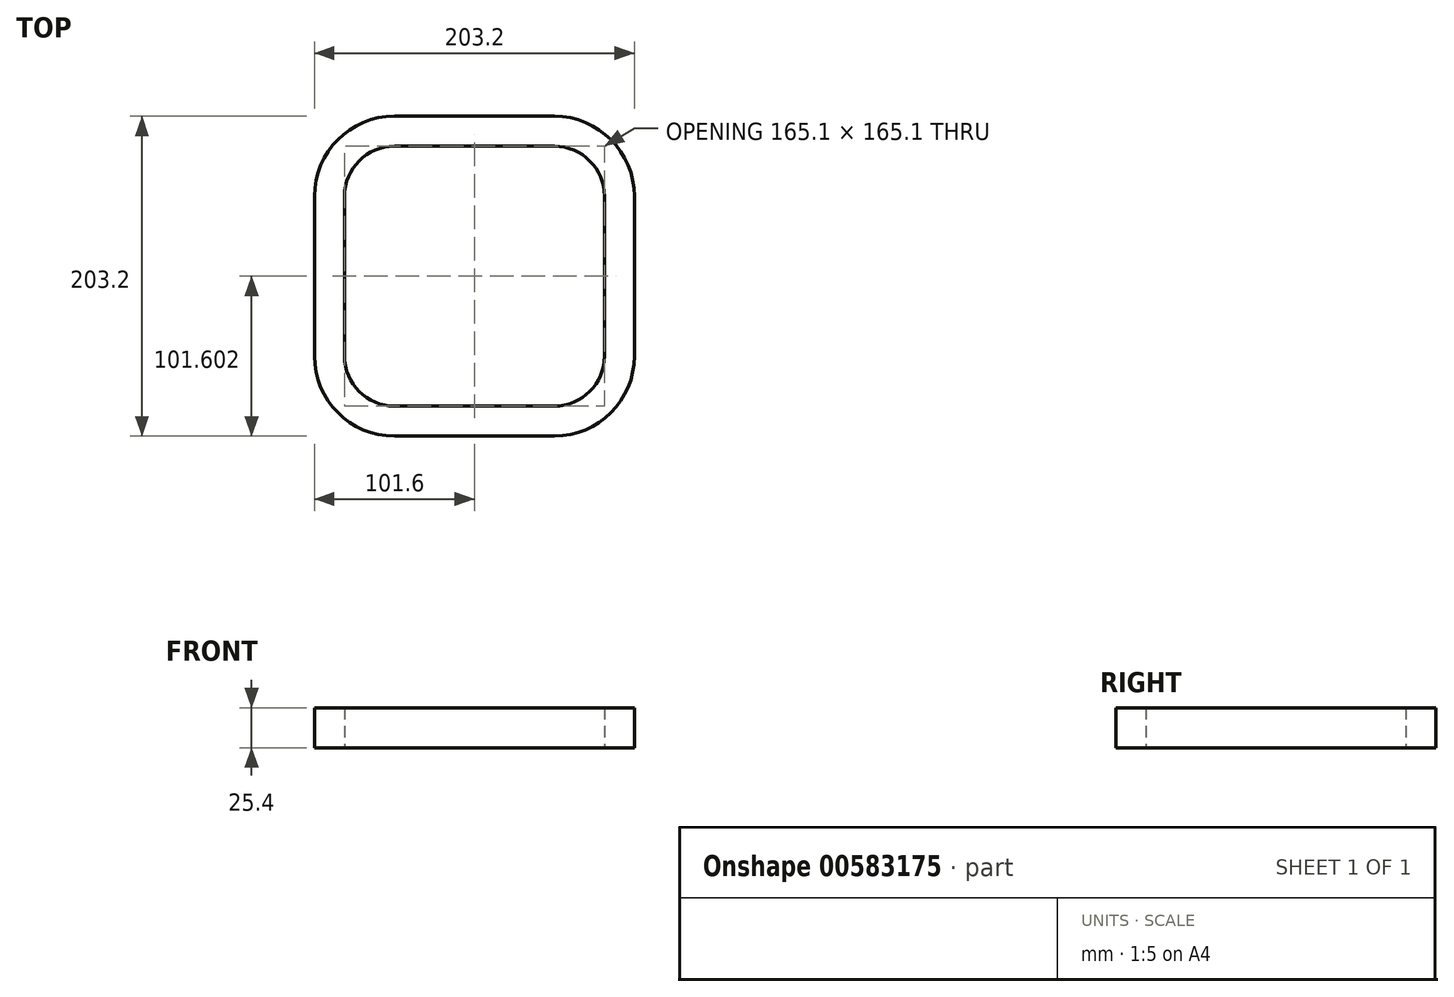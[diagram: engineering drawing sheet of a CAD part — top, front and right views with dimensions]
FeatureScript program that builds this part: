
annotation { "Feature Type Name" : "Feature", "Feature Type Description" : "" }
export const myFeature = defineFeature(function(context is Context, id is Id, definition is map)
    precondition{}
    {
        {
            var Q0;
            Q0=qCreatedBy(makeId("Top.planeOp"),FACE);
            var sketch = newSketch(context, id + "F0", { "sketchPlane" : qUnion([Q0])});
            skLineSegment(sketch, "E0.bottom", {"start": v(-116.13, 166.11) * mm, "end": v(-14.53, 166.11) * mm});
            skLineSegment(sketch, "E0.top", {"start": v(-116.13, -37.09) * mm, "end": v(-14.53, -37.09) * mm});
            skLineSegment(sketch, "E0.left", {"start": v(-166.93, 115.31) * mm, "end": v(-166.93, 13.71) * mm});
            skLineSegment(sketch, "E0.right", {"start": v(36.27, 115.31) * mm, "end": v(36.27, 13.71) * mm});
            skPoint(sketch, "E1.visualSharp", {"position": v(-166.93, 166.11) * mm});
            skArc(sketch, "E1.filletArc", {"start": v(-116.13, 166.11) * mm, "mid": v(-152.05, 151.23) * mm, "end": v(-166.93, 115.31) * mm});
            skPoint(sketch, "E2.visualSharp", {"position": v(-166.93, -37.09) * mm});
            skArc(sketch, "E2.filletArc", {"start": v(-166.93, 13.71) * mm, "mid": v(-152.05, -22.2) * mm, "end": v(-116.13, -37.09) * mm});
            skPoint(sketch, "E3.visualSharp", {"position": v(36.27, -37.09) * mm});
            skArc(sketch, "E3.filletArc", {"start": v(-14.53, -37.09) * mm, "mid": v(21.4, -22.2) * mm, "end": v(36.27, 13.71) * mm});
            skPoint(sketch, "E4.visualSharp", {"position": v(36.27, 166.11) * mm});
            skArc(sketch, "E4.filletArc", {"start": v(36.27, 115.31) * mm, "mid": v(21.4, 151.23) * mm, "end": v(-14.53, 166.11) * mm});
            skLineSegment(sketch, "E5.0", {"start": v(17.22, 115.31) * mm, "end": v(17.22, 13.71) * mm});
            skArc(sketch, "E5.1", {"start": v(-14.53, -18.04) * mm, "mid": v(7.92, -8.74) * mm, "end": v(17.22, 13.71) * mm});
            skArc(sketch, "E5.2", {"start": v(17.22, 115.31) * mm, "mid": v(7.92, 137.76) * mm, "end": v(-14.53, 147.06) * mm});
            skLineSegment(sketch, "E5.3", {"start": v(-116.13, -18.04) * mm, "end": v(-14.53, -18.04) * mm});
            skLineSegment(sketch, "E5.4", {"start": v(-116.13, 147.06) * mm, "end": v(-14.53, 147.06) * mm});
            skArc(sketch, "E5.5", {"start": v(-116.13, 147.06) * mm, "mid": v(-138.58, 137.76) * mm, "end": v(-147.88, 115.31) * mm});
            skLineSegment(sketch, "E5.6", {"start": v(-147.88, 115.31) * mm, "end": v(-147.88, 13.71) * mm});
            skArc(sketch, "E5.7", {"start": v(-147.88, 13.71) * mm, "mid": v(-138.58, -8.74) * mm, "end": v(-116.13, -18.04) * mm});
            skSolve(sketch);
        }
        {
            var Q0;
            Q0=makeQuery(id+"F0.imprint","IMPRINT",FACE,{"disambiguationData":[TD([[makeQuery(id+"F0.imprint","IMPRINT",EDGE,{"derivedFrom":sQuery(id+"F0.wireOp",EDGE,"E0.bottom")}),-1.0]])]});
            extrude(context, id + "F1", {"entities" : qUnion([Q0]), "depth" : 25.4 * mm, "offsetDistance" : 25.4 * mm});
        }
    });
